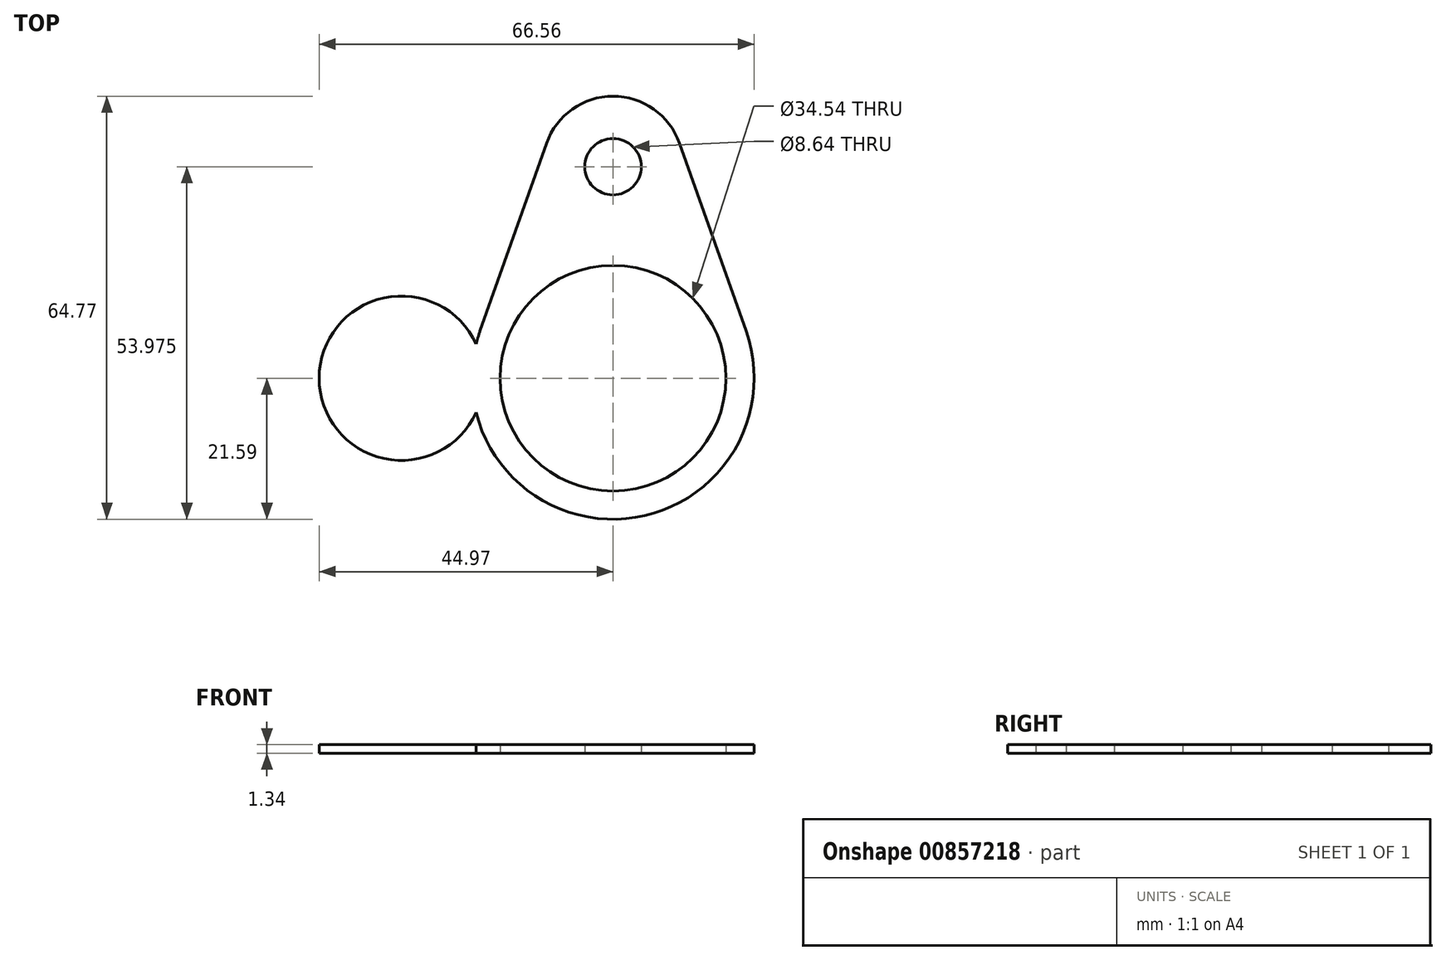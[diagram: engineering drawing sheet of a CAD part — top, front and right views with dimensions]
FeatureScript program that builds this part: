
annotation { "Feature Type Name" : "Feature", "Feature Type Description" : "" }
export const myFeature = defineFeature(function(context is Context, id is Id, definition is map)
    precondition{}
    {
        {
            assignVariable(context, id + "F0", {"name" : "DiaMayor", "anyValue" : 1.7});
        }
        {
            var Q0;
            Q0=qCreatedBy(makeId("Top.planeOp"),FACE);
            var sketch = newSketch(context, id + "F1", { "sketchPlane" : qUnion([Q0])});
            skCircle(sketch, "E0", {"center": v(0, 0) * mm, "radius": 21.59 * mm});
            skLineSegment(sketch, "E1", {"start": v(0, 0) * mm, "end": v(0, 32.38) * mm});
            skCircle(sketch, "E2", {"center": v(0, 32.39) * mm, "radius": 10.8 * mm});
            skLineSegment(sketch, "E3", {"start": v(-10.18, 35.98) * mm, "end": v(-20.36, 7.2) * mm});
            skLineSegment(sketch, "E4", {"start": v(10.18, 35.98) * mm, "end": v(20.36, 7.2) * mm});
            skLineSegment(sketch, "E5", {"start": v(0, 0) * mm, "end": v(-32.39, 0) * mm});
            skCircle(sketch, "E6", {"center": v(-32.39, 0) * mm, "radius": 12.59 * mm});
            skCircle(sketch, "E7", {"center": v(0, 0) * mm, "radius": 17.27 * mm});
            skCircle(sketch, "E8", {"center": v(0, 32.39) * mm, "radius": 4.32 * mm});
            skSolve(sketch);
        }
        {
            var Q0;
            Q0 = qSketchRegion(id + "F1", true);
            extrude(context, id + "F2", {"entities" : qUnion([Q0]), "depth" : ((getVariable(context, 'DiaMayor') / 5) + 1) * mm, "offsetDistance" : 25.4 * mm});
        }
    });
